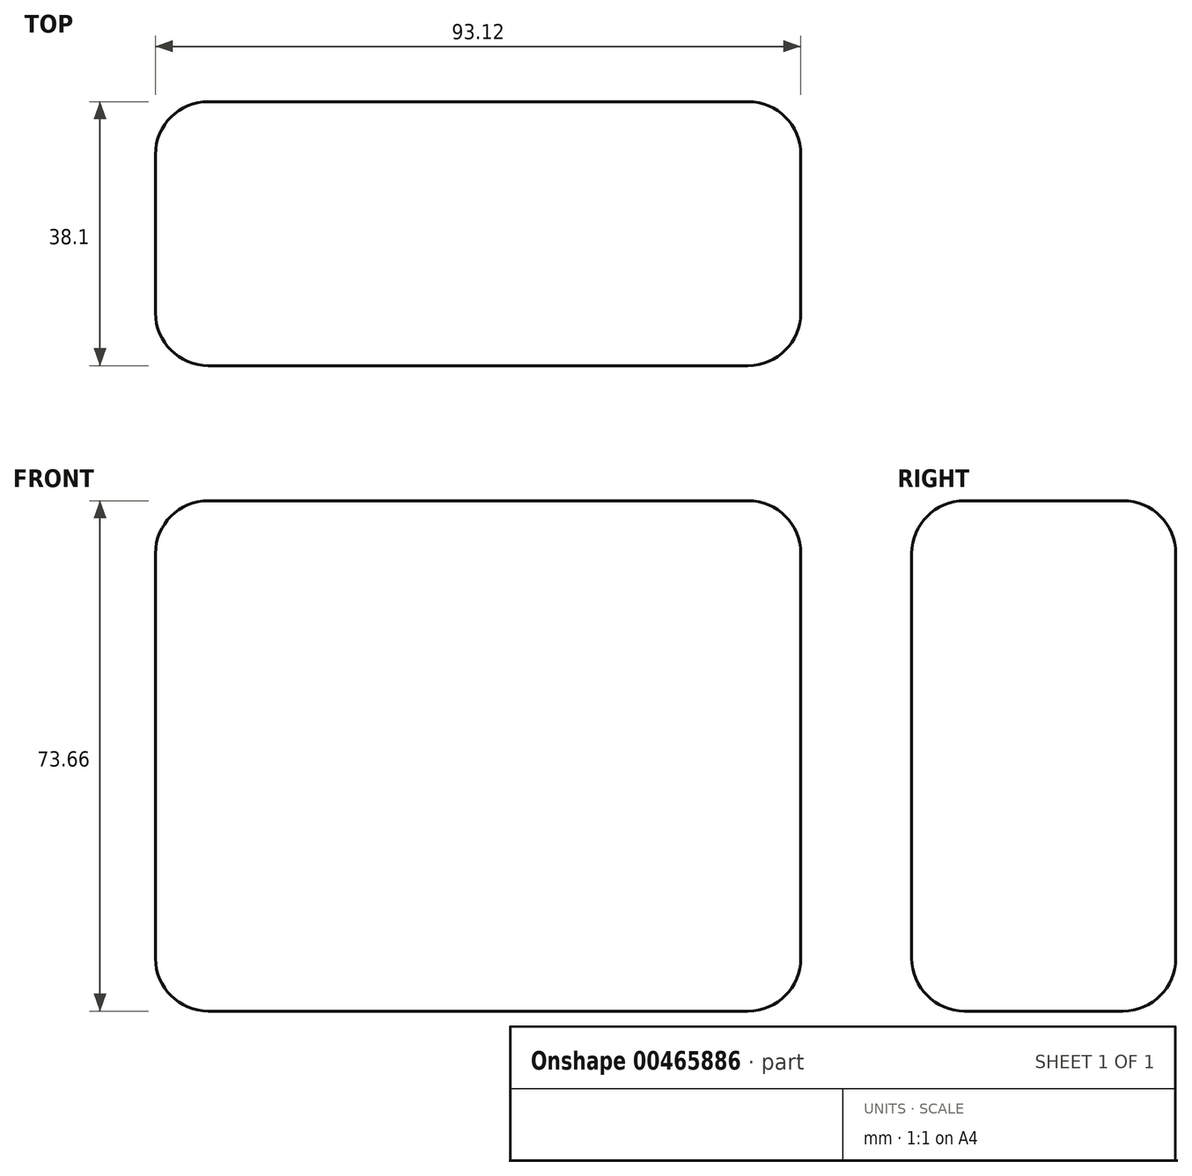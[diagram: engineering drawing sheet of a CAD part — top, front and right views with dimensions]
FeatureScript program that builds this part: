
annotation { "Feature Type Name" : "Feature", "Feature Type Description" : "" }
export const myFeature = defineFeature(function(context is Context, id is Id, definition is map)
    precondition{}
    {
        {
            var Q0;
            Q0=qCreatedBy(makeId("Front.planeOp"),FACE);
            var sketch = newSketch(context, id + "F0", { "sketchPlane" : qUnion([Q0])});
            skLineSegment(sketch, "E0.bottom", {"start": v(-46.56, 36.83) * mm, "end": v(46.56, 36.83) * mm});
            skLineSegment(sketch, "E0.top", {"start": v(-46.56, -36.83) * mm, "end": v(46.56, -36.83) * mm});
            skLineSegment(sketch, "E0.left", {"start": v(-46.56, 36.83) * mm, "end": v(-46.56, -36.83) * mm});
            skLineSegment(sketch, "E0.right", {"start": v(46.56, 36.83) * mm, "end": v(46.56, -36.83) * mm});
            skPoint(sketch, "E0.middle", {"position": v(0, 0) * mm});
            skSolve(sketch);
        }
        {
            var Q0;
            Q0=makeQuery(id+"F0.imprint","IMPRINT",FACE,{"disambiguationData":[TD([[makeQuery(id+"F0.imprint","IMPRINT",EDGE,{"derivedFrom":sQuery(id+"F0.wireOp",EDGE,"E0.bottom")}),-1.0]])]});
            extrude(context, id + "F1", {"entities" : qUnion([Q0]), "endBound" : BoundingType.SYMMETRIC, "depth" : 38.1 * mm, "offsetDistance" : 25.4 * mm});
        }
        {
            var Q0;
            Q0=makeQuery(id+"F1.opExtrude","SWEPT_EDGE",EDGE,{"disambiguationData":[OSD([sQuery(id+"F0.wireOp",EDGE,"E0.top"),sQuery(id+"F0.wireOp",EDGE,"E0.left")])]});
            var Q1;
            Q1=makeQuery(id+"F1.opExtrude","SWEPT_EDGE",EDGE,{"disambiguationData":[OSD([sQuery(id+"F0.wireOp",EDGE,"E0.bottom"),sQuery(id+"F0.wireOp",EDGE,"E0.left")])]});
            var Q2;
            Q2=makeQuery(id+"F1.opExtrude","SWEPT_EDGE",EDGE,{"disambiguationData":[OSD([sQuery(id+"F0.wireOp",EDGE,"E0.top"),sQuery(id+"F0.wireOp",EDGE,"E0.right")])]});
            var Q3;
            Q3=makeQuery(id+"F1.opExtrude","SWEPT_EDGE",EDGE,{"disambiguationData":[OSD([sQuery(id+"F0.wireOp",EDGE,"E0.bottom"),sQuery(id+"F0.wireOp",EDGE,"E0.right")])]});
            fillet(context, id + "F2", {"entities" : qUnion([Q0, Q1, Q2, Q3]), "radius" : 7.62 * mm, "tangentPropagation" : true, "allowEdgeOverflow" : false});
        }
        {
            var Q0;
            {var subQ0=sQuery(id+"F0.wireOp",EDGE,"E0.right");var subQ1=sQuery(id+"F0.wireOp",EDGE,"E0.top");Q0=makeQuery(id+"F2.opFillet","BLEND_EDGE",EDGE,{"blendedFrom":[makeQuery(id+"F1.opExtrude","SWEPT_EDGE",EDGE,{"disambiguationData":[OSD([subQ1,subQ0])]}),makeQuery(id+"F1.opExtrude","CAP_FACE",FACE,{"disambiguationData":[OSD([sQuery(id+"F0.wireOp",EDGE,"E0.bottom"),subQ1,sQuery(id+"F0.wireOp",EDGE,"E0.left"),subQ0])],"isStart":false})],"blendedInto":[makeQuery(id+"F1.opExtrude","CAP_FACE",FACE,{"disambiguationData":[OSD([sQuery(id+"F0.wireOp",EDGE,"E0.bottom"),subQ1,sQuery(id+"F0.wireOp",EDGE,"E0.left"),subQ0])],"isStart":false})]});}
            var Q1;
            Q1=makeQuery(id+"F1.opExtrude","CAP_EDGE",EDGE,{"disambiguationData":[OSD([sQuery(id+"F0.wireOp",EDGE,"E0.top")])],"isStart":false});
            var Q2;
            Q2=makeQuery(id+"F1.opExtrude","CAP_EDGE",EDGE,{"disambiguationData":[OSD([sQuery(id+"F0.wireOp",EDGE,"E0.right")])],"isStart":false});
            var Q3;
            {var subQ0=sQuery(id+"F0.wireOp",EDGE,"E0.right");var subQ1=sQuery(id+"F0.wireOp",EDGE,"E0.bottom");Q3=makeQuery(id+"F2.opFillet","BLEND_EDGE",EDGE,{"blendedFrom":[makeQuery(id+"F1.opExtrude","SWEPT_EDGE",EDGE,{"disambiguationData":[OSD([subQ1,subQ0])]}),makeQuery(id+"F1.opExtrude","CAP_FACE",FACE,{"disambiguationData":[OSD([subQ1,sQuery(id+"F0.wireOp",EDGE,"E0.top"),sQuery(id+"F0.wireOp",EDGE,"E0.left"),subQ0])],"isStart":false})],"blendedInto":[makeQuery(id+"F1.opExtrude","CAP_FACE",FACE,{"disambiguationData":[OSD([subQ1,sQuery(id+"F0.wireOp",EDGE,"E0.top"),sQuery(id+"F0.wireOp",EDGE,"E0.left"),subQ0])],"isStart":false})]});}
            var Q4;
            Q4=makeQuery(id+"F1.opExtrude","CAP_EDGE",EDGE,{"disambiguationData":[OSD([sQuery(id+"F0.wireOp",EDGE,"E0.bottom")])],"isStart":false});
            var Q5;
            {var subQ0=sQuery(id+"F0.wireOp",EDGE,"E0.left");var subQ1=sQuery(id+"F0.wireOp",EDGE,"E0.bottom");Q5=makeQuery(id+"F2.opFillet","BLEND_EDGE",EDGE,{"blendedFrom":[makeQuery(id+"F1.opExtrude","SWEPT_EDGE",EDGE,{"disambiguationData":[OSD([subQ1,subQ0])]}),makeQuery(id+"F1.opExtrude","CAP_FACE",FACE,{"disambiguationData":[OSD([subQ1,sQuery(id+"F0.wireOp",EDGE,"E0.top"),subQ0,sQuery(id+"F0.wireOp",EDGE,"E0.right")])],"isStart":false})],"blendedInto":[makeQuery(id+"F1.opExtrude","CAP_FACE",FACE,{"disambiguationData":[OSD([subQ1,sQuery(id+"F0.wireOp",EDGE,"E0.top"),subQ0,sQuery(id+"F0.wireOp",EDGE,"E0.right")])],"isStart":false})]});}
            var Q6;
            Q6=makeQuery(id+"F1.opExtrude","CAP_EDGE",EDGE,{"disambiguationData":[OSD([sQuery(id+"F0.wireOp",EDGE,"E0.left")])],"isStart":false});
            var Q7;
            {var subQ0=sQuery(id+"F0.wireOp",EDGE,"E0.left");var subQ1=sQuery(id+"F0.wireOp",EDGE,"E0.top");Q7=makeQuery(id+"F2.opFillet","BLEND_EDGE",EDGE,{"blendedFrom":[makeQuery(id+"F1.opExtrude","SWEPT_EDGE",EDGE,{"disambiguationData":[OSD([subQ1,subQ0])]}),makeQuery(id+"F1.opExtrude","CAP_FACE",FACE,{"disambiguationData":[OSD([sQuery(id+"F0.wireOp",EDGE,"E0.bottom"),subQ1,subQ0,sQuery(id+"F0.wireOp",EDGE,"E0.right")])],"isStart":false})],"blendedInto":[makeQuery(id+"F1.opExtrude","CAP_FACE",FACE,{"disambiguationData":[OSD([sQuery(id+"F0.wireOp",EDGE,"E0.bottom"),subQ1,subQ0,sQuery(id+"F0.wireOp",EDGE,"E0.right")])],"isStart":false})]});}
            fillet(context, id + "F3", {"entities" : qUnion([Q0, Q1, Q2, Q3, Q4, Q5, Q6, Q7]), "radius" : 7.62 * mm, "tangentPropagation" : true, "allowEdgeOverflow" : false});
        }
        {
            var Q0;
            {var subQ0=sQuery(id+"F0.wireOp",EDGE,"E0.right");var subQ1=sQuery(id+"F0.wireOp",EDGE,"E0.top");Q0=makeQuery(id+"F2.opFillet","BLEND_EDGE",EDGE,{"blendedFrom":[makeQuery(id+"F1.opExtrude","SWEPT_EDGE",EDGE,{"disambiguationData":[OSD([subQ1,subQ0])]}),makeQuery(id+"F1.opExtrude","CAP_FACE",FACE,{"disambiguationData":[OSD([sQuery(id+"F0.wireOp",EDGE,"E0.bottom"),subQ1,sQuery(id+"F0.wireOp",EDGE,"E0.left"),subQ0])],"isStart":true})],"blendedInto":[makeQuery(id+"F1.opExtrude","CAP_FACE",FACE,{"disambiguationData":[OSD([sQuery(id+"F0.wireOp",EDGE,"E0.bottom"),subQ1,sQuery(id+"F0.wireOp",EDGE,"E0.left"),subQ0])],"isStart":true})]});}
            var Q1;
            Q1=makeQuery(id+"F1.opExtrude","CAP_EDGE",EDGE,{"disambiguationData":[OSD([sQuery(id+"F0.wireOp",EDGE,"E0.top")])],"isStart":true});
            var Q2;
            Q2=makeQuery(id+"F1.opExtrude","CAP_EDGE",EDGE,{"disambiguationData":[OSD([sQuery(id+"F0.wireOp",EDGE,"E0.right")])],"isStart":true});
            var Q3;
            {var subQ0=sQuery(id+"F0.wireOp",EDGE,"E0.left");var subQ1=sQuery(id+"F0.wireOp",EDGE,"E0.top");Q3=makeQuery(id+"F2.opFillet","BLEND_EDGE",EDGE,{"blendedFrom":[makeQuery(id+"F1.opExtrude","SWEPT_EDGE",EDGE,{"disambiguationData":[OSD([subQ1,subQ0])]}),makeQuery(id+"F1.opExtrude","CAP_FACE",FACE,{"disambiguationData":[OSD([sQuery(id+"F0.wireOp",EDGE,"E0.bottom"),subQ1,subQ0,sQuery(id+"F0.wireOp",EDGE,"E0.right")])],"isStart":true})],"blendedInto":[makeQuery(id+"F1.opExtrude","CAP_FACE",FACE,{"disambiguationData":[OSD([sQuery(id+"F0.wireOp",EDGE,"E0.bottom"),subQ1,subQ0,sQuery(id+"F0.wireOp",EDGE,"E0.right")])],"isStart":true})]});}
            var Q4;
            Q4=makeQuery(id+"F1.opExtrude","CAP_EDGE",EDGE,{"disambiguationData":[OSD([sQuery(id+"F0.wireOp",EDGE,"E0.left")])],"isStart":true});
            var Q5;
            {var subQ0=sQuery(id+"F0.wireOp",EDGE,"E0.left");var subQ1=sQuery(id+"F0.wireOp",EDGE,"E0.bottom");Q5=makeQuery(id+"F2.opFillet","BLEND_EDGE",EDGE,{"blendedFrom":[makeQuery(id+"F1.opExtrude","SWEPT_EDGE",EDGE,{"disambiguationData":[OSD([subQ1,subQ0])]}),makeQuery(id+"F1.opExtrude","CAP_FACE",FACE,{"disambiguationData":[OSD([subQ1,sQuery(id+"F0.wireOp",EDGE,"E0.top"),subQ0,sQuery(id+"F0.wireOp",EDGE,"E0.right")])],"isStart":true})],"blendedInto":[makeQuery(id+"F1.opExtrude","CAP_FACE",FACE,{"disambiguationData":[OSD([subQ1,sQuery(id+"F0.wireOp",EDGE,"E0.top"),subQ0,sQuery(id+"F0.wireOp",EDGE,"E0.right")])],"isStart":true})]});}
            var Q6;
            Q6=makeQuery(id+"F1.opExtrude","CAP_EDGE",EDGE,{"disambiguationData":[OSD([sQuery(id+"F0.wireOp",EDGE,"E0.bottom")])],"isStart":true});
            var Q7;
            {var subQ0=sQuery(id+"F0.wireOp",EDGE,"E0.right");var subQ1=sQuery(id+"F0.wireOp",EDGE,"E0.bottom");Q7=makeQuery(id+"F2.opFillet","BLEND_EDGE",EDGE,{"blendedFrom":[makeQuery(id+"F1.opExtrude","SWEPT_EDGE",EDGE,{"disambiguationData":[OSD([subQ1,subQ0])]}),makeQuery(id+"F1.opExtrude","CAP_FACE",FACE,{"disambiguationData":[OSD([subQ1,sQuery(id+"F0.wireOp",EDGE,"E0.top"),sQuery(id+"F0.wireOp",EDGE,"E0.left"),subQ0])],"isStart":true})],"blendedInto":[makeQuery(id+"F1.opExtrude","CAP_FACE",FACE,{"disambiguationData":[OSD([subQ1,sQuery(id+"F0.wireOp",EDGE,"E0.top"),sQuery(id+"F0.wireOp",EDGE,"E0.left"),subQ0])],"isStart":true})]});}
            fillet(context, id + "F4", {"entities" : qUnion([Q0, Q1, Q2, Q3, Q4, Q5, Q6, Q7]), "radius" : 7.62 * mm, "tangentPropagation" : true, "allowEdgeOverflow" : false});
        }
    });
